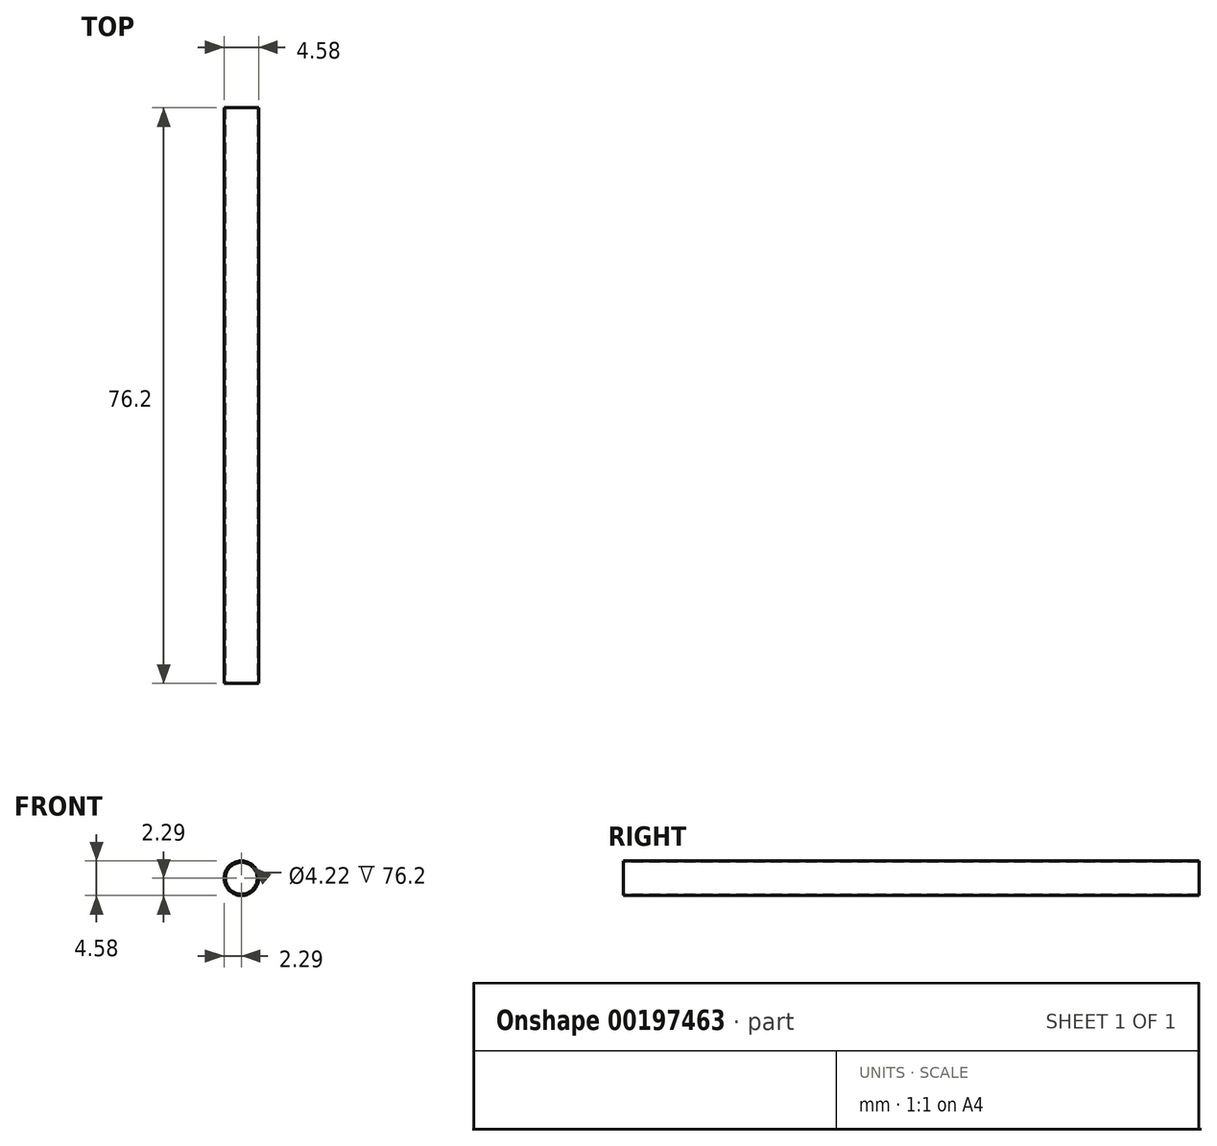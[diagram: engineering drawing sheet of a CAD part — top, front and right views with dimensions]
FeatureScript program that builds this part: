
annotation { "Feature Type Name" : "Feature", "Feature Type Description" : "" }
export const myFeature = defineFeature(function(context is Context, id is Id, definition is map)
    precondition{}
    {
        {
            var Q0;
            Q0=qCreatedBy(makeId("Front.planeOp"),FACE);
            var sketch = newSketch(context, id + "F0", { "sketchPlane" : qUnion([Q0])});
            skCircle(sketch, "E0", {"center": v(0, 0) * mm, "radius": 2.29 * mm});
            skCircle(sketch, "E1", {"center": v(0, 0) * mm, "radius": 2.1 * mm});
            skSolve(sketch);
        }
        {
            var Q0;
            Q0 = qSketchRegion(id + "F0", true);
            extrude(context, id + "F1", {"entities" : qUnion([Q0]), "oppositeDirection" : true, "depth" : 76.2 * mm});
        }
    });
